# Revit family: Vitreous china wall-hung bide-Element-357575xx0
name_source: partatom
category: Plumbing Fixtures
revit_build: Autodesk Revit Architecture 2014 (Build: 20130308_1515(x64)
units: mm (PartAtom-declared; Revit-internal decimal feet)

## types (4) — shared parameters
BIMobject category = Bidets
Description = Vitreous china wall-hung bidet
Drain Diameter = 46 mm  [stored 0.150919 ft]
Edition number = 1
Height = 280 mm  [stored 0.918635 ft]
IFC Classification = Sanitary Terminal
Installation instructions = http://www.roca.com
Installation type = Wall-hung
Length = 370 mm  [stored 1.21391 ft]
Manufacturer URL = www.roca.com
Manufacturer name = Roca
Model = 357575..0
NBS Reference Code = 35-06-11
NBS Reference Description = Bidets
Nominal height = 28000
Nominal width = 54500
OmniClass Code = 23-31 23 00
OmniClass Description = Bidets
Product Guid = 259fec59-0210-48ce-ab34-be78fb3b164b
Product data url = http://bimobject.com
Product family = Element
Product group = BIDETS
QR code = http://bimobject.com
Secondary Material = Chrome - Element - Roca
Shape = Square
Taphole Diameter = 30 mm  [stored 0.0984252 ft]
Taphole configuration = 1 Prepunched
Technical description = http://www.roca.com
UNSPSC Code = 30181502
URL = http://www.export.roca.com
Uniclass 1.4 Code = L7215
Uniclass 1.4 Description = Bidets
Uniclass 2.0 Code = PR-35-06-11
Uniclass 2.0 Description = Bidets
Width = 545 mm  [stored 1.78806 ft]
zero-valued in all types: Weight Net (Kg)

## per-type parameters (varying)
| type | Imported Category Visibility 01 | Imported Category Visibility 02 | Imported Category Visibility 03 | Imported Category Visibility 04 | Primary Material | Product SKU |
| 357575000 White | Yes | No | No | No | White-Element-Roca | 357575000 |
| 357575170 Pergamon | No | Yes | No | No | Pergamon - Element - Roca | 357575170 |
| 357575910 Edelweiss | No | No | Yes | No | Edelweiss-Element-Roca | 357575910 |
| 357575920 Graphit | No | No | No | Yes | Graphit-Element-Roca | 357575920 |

note: [stored X ft] marks values corroborated as IEEE doubles in the binary element streams (Revit-internal decimal feet)

## geometry (parser evidence)
native form markers: Blend x2, Sweep x5
no freeform markers — native parametric forms only
